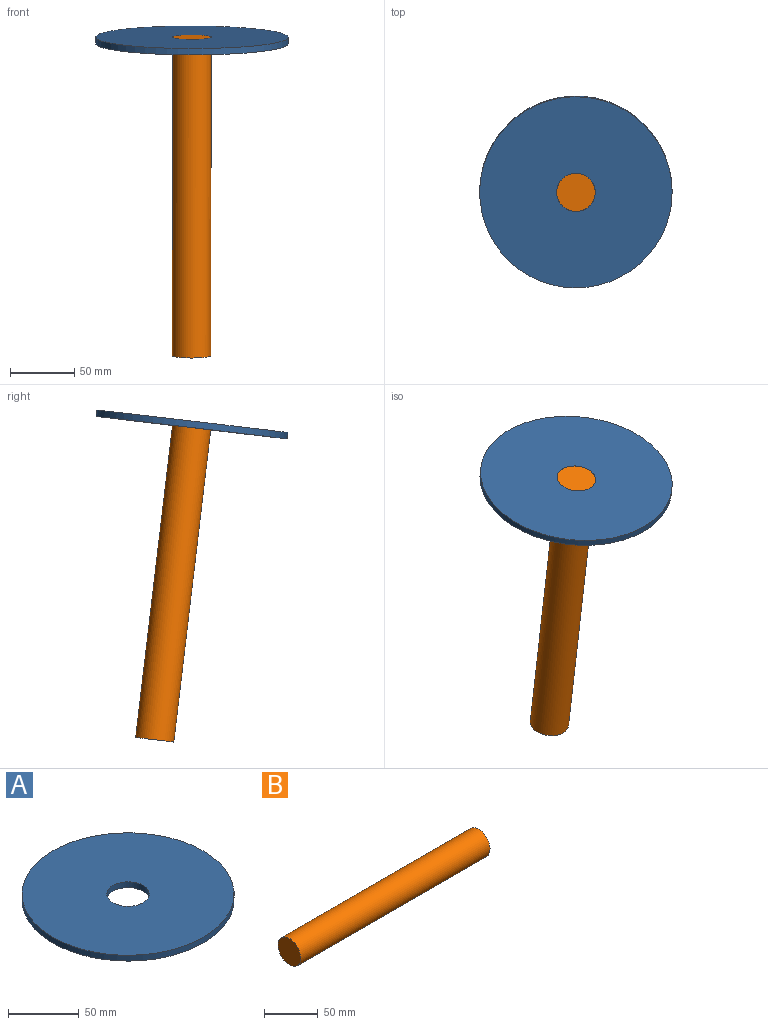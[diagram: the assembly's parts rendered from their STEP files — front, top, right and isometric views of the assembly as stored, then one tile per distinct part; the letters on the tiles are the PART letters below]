
ASSEMBLY  parts=2 mates=1
PART A: 4 faces, bbox 150x150x5 mm
  f0: cylinder r=15mm len=30mm, axis (0,0,-1), area 471.2mm2, adj f2,f3
  f1: cylinder r=75mm len=150mm, axis (0,0,-1), area 2356.2mm2, adj f2,f3
  f2: plane 150x150mm, normal (0,0,1), area 16964.6mm2, adj f0,f1
  f3: plane 150x150mm, normal (0,0,-1), area 16964.6mm2, adj f0,f1
PART B: 3 faces, bbox 250x30x30 mm
  f0: cylinder r=15mm len=250mm, axis (-1,0,0), area 23561.9mm2, adj f1,f2
  f1: plane 30x30mm, normal (1,0,0), area 706.9mm2, adj f0
  f2: plane 30x30mm, normal (-1,0,0), area 706.9mm2, adj f0
PLACE A rot(axis=(0.99,0.01,0.1),6.8deg) t=(327.58,95.46,57.82)mm
PLACE B rot(axis=(0.6,0.6,-0.53),123.6deg) t=(327.59,94.87,62.79)mm
MATE ball A.f0 <-> B.f0  axis (0,-0.12,0.99) through (327.59,94.87,62.79)mm
